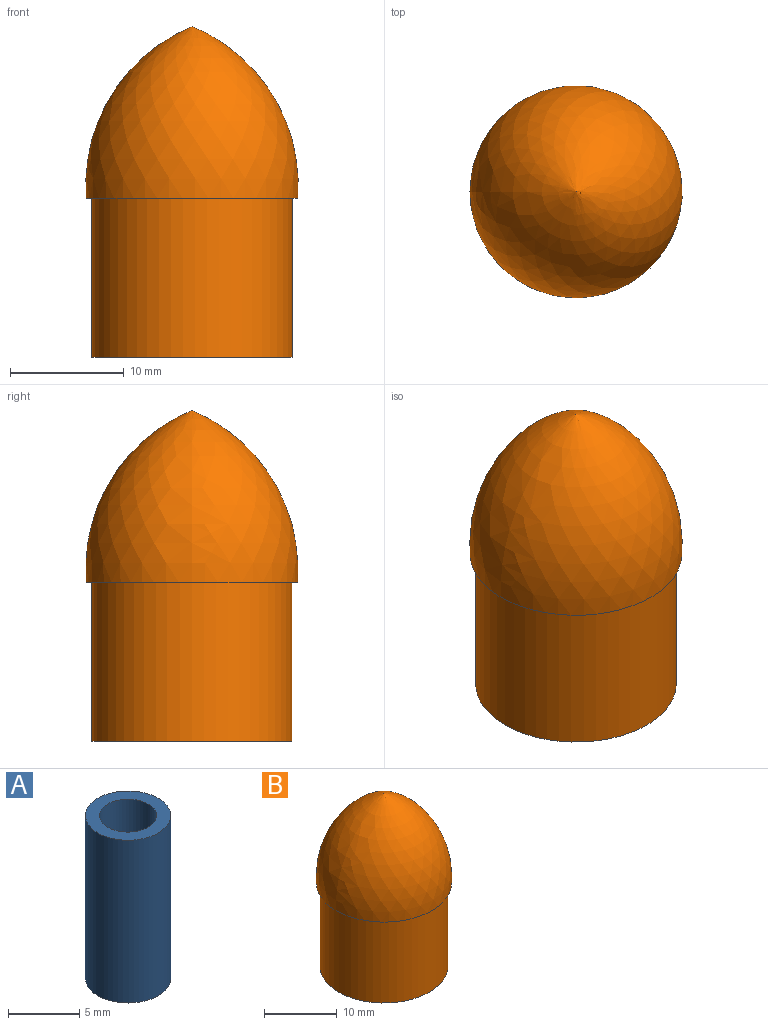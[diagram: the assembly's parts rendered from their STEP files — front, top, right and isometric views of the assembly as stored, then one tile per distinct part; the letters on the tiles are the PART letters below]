
ASSEMBLY  parts=2 mates=1
PART A: 4 faces, bbox 6x6x14 mm
  f0: cylinder r=2mm len=14mm, axis (0,0,-1), area 175.9mm2, adj f2,f3
  f1: cylinder r=3mm len=14mm, axis (0,0,-1), area 263.9mm2, adj f2,f3
  f2: plane 6x6mm, normal (0,0,1), area 15.7mm2, adj f0,f1
  f3: plane 6x6mm, normal (0,0,-1), area 15.7mm2, adj f0,f1
PART B: 7 faces, bbox 18.7x18.7x29.1 mm
  f0: revolved ~17.18x17.18mm, area 604.2mm2, adj f1
  f1: plane 17.18x17.18mm, normal (0,0,1), area 28.1mm2, adj f0,f2
  f2: cylinder r=8.05mm len=16.1mm, axis (0,0,-1), area 746mm2, adj f1,f3
  f3: plane 17.6x17.6mm, normal (0,0,-1), area 39.7mm2, adj f2,f4
  f4: cylinder r=8.8mm len=17.6mm, axis (0,0,-1), area 774.1mm2, adj f3,f5
  f5: plane 18.6x18.6mm, normal (0,0,-1), area 28.4mm2, adj f4,f6
  f6: revolved ~18.69x18.69mm, area 746mm2, adj f5
PLACE A t=(-1.8,4.39,6.83)mm
PLACE B t=(-7.3,4.39,5.9)mm
MATE planar A.f0 <-> B.f2  axis (0,0,-1) through (-1.8,4.39,6.83)mm
